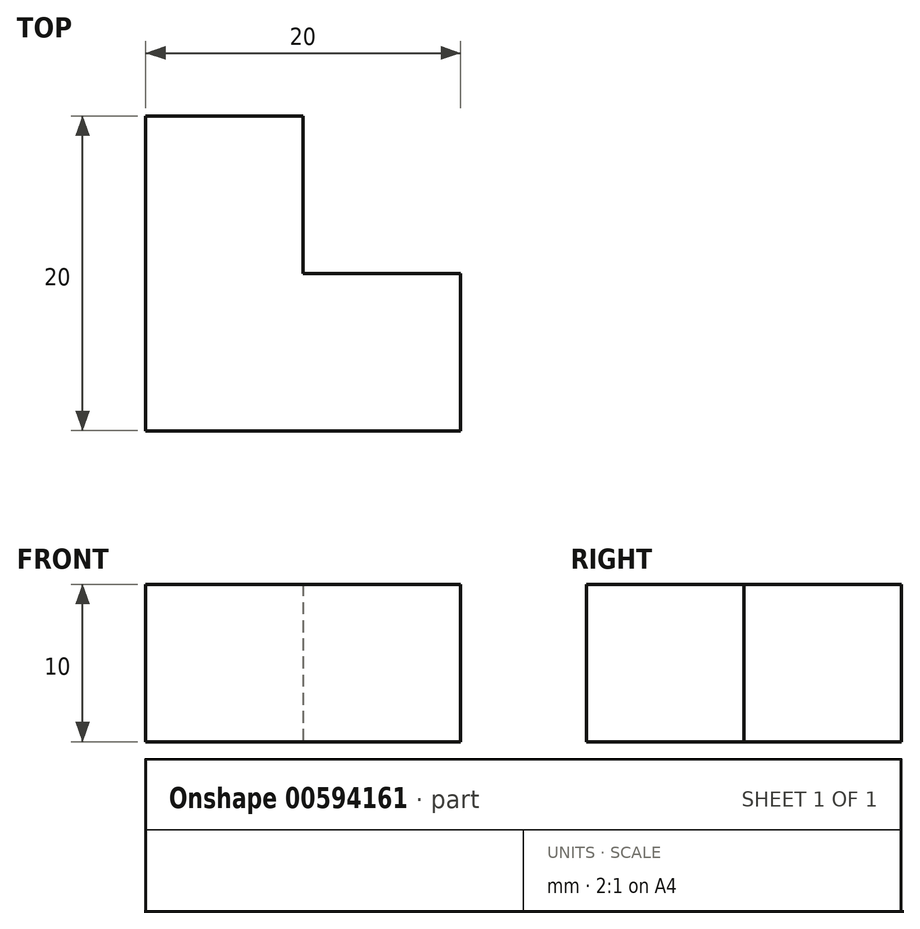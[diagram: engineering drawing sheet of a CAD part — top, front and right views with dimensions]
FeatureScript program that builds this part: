
annotation { "Feature Type Name" : "Feature", "Feature Type Description" : "" }
export const myFeature = defineFeature(function(context is Context, id is Id, definition is map)
    precondition{}
    {
        {
            var Q0;
            Q0=qCreatedBy(makeId("Top.planeOp"),FACE);
            var sketch = newSketch(context, id + "F0", { "sketchPlane" : qUnion([Q0])});
            skLineSegment(sketch, "E0", {"start": v(3.06, 7.22) * mm, "end": v(13.06, 7.22) * mm});
            skLineSegment(sketch, "E1", {"start": v(13.06, 7.22) * mm, "end": v(13.06, -2.78) * mm});
            skLineSegment(sketch, "E2", {"start": v(13.06, -2.78) * mm, "end": v(23.06, -2.78) * mm});
            skLineSegment(sketch, "E3", {"start": v(23.06, -2.78) * mm, "end": v(23.06, -12.78) * mm});
            skLineSegment(sketch, "E4", {"start": v(23.06, -12.78) * mm, "end": v(3.06, -12.78) * mm});
            skLineSegment(sketch, "E5", {"start": v(3.06, -12.78) * mm, "end": v(3.06, 7.22) * mm});
            skSolve(sketch);
        }
        {
            var Q0;
            Q0=makeQuery(id+"F0.imprint","IMPRINT",FACE,{"disambiguationData":[TD([[makeQuery(id+"F0.imprint","IMPRINT",EDGE,{"derivedFrom":sQuery(id+"F0.wireOp",EDGE,"E0")}),-1.0]])]});
            extrude(context, id + "F1", {"entities" : qUnion([Q0]), "depth" : 10 * mm, "offsetDistance" : 25 * mm});
        }
    });
